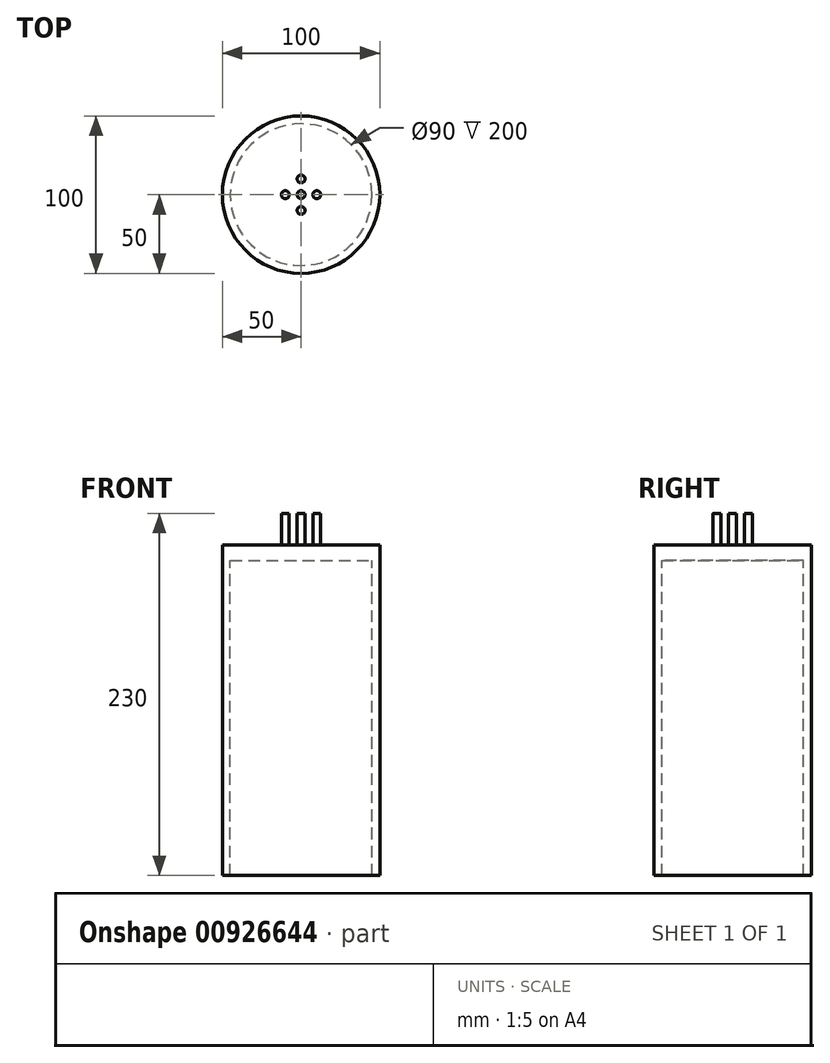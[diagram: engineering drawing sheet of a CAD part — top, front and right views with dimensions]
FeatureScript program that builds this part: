
annotation { "Feature Type Name" : "Feature", "Feature Type Description" : "" }
export const myFeature = defineFeature(function(context is Context, id is Id, definition is map)
    precondition{}
    {
        {
            var Q0;
            Q0=qCreatedBy(makeId("Top.planeOp"),FACE);
            var sketch = newSketch(context, id + "F0", { "sketchPlane" : qUnion([Q0])});
            skCircle(sketch, "E0", {"center": v(0, 0) * mm, "radius": 50 * mm});
            skSolve(sketch);
        }
        {
            var Q0;
            Q0=makeQuery(id+"F0.imprint","IMPRINT",FACE,{"disambiguationData":[TD([[makeQuery(id+"F0.imprint","IMPRINT",EDGE,{"derivedFrom":sQuery(id+"F0.wireOp",EDGE,"E0")}),1.0]])]});
            extrude(context, id + "F1", {"entities" : qUnion([Q0]), "depth" : 10 * mm, "offsetDistance" : 25 * mm});
        }
        {
            var Q0;
            Q0=makeQuery(id+"F1.opExtrude","CAP_FACE",FACE,{"disambiguationData":[OSD([sQuery(id+"F0.wireOp",EDGE,"E0")])],"isStart":true});
            var sketch = newSketch(context, id + "F2", { "sketchPlane" : qUnion([Q0])});
            skCircle(sketch, "E1", {"center": v(0, 0) * mm, "radius": 45 * mm});
            skSolve(sketch);
        }
        {
            var Q0;
            Q0=makeQuery(id+"F2.imprint","IMPRINT",FACE,{"disambiguationData":[TD([[makeQuery(id+"F2.imprint","IMPRINT",EDGE,{"derivedFrom":sQuery(id+"F2.wireOp",EDGE,"E1")}),-1.0]])]});
            extrude(context, id + "F3", {"entities" : qUnion([Q0]), "operationType" : NewBodyOperationType.ADD, "depth" : 200 * mm, "offsetDistance" : 25 * mm});
        }
        {
            var Q0;
            Q0=makeQuery(id+"F1.opExtrude","CAP_FACE",FACE,{"disambiguationData":[OSD([sQuery(id+"F0.wireOp",EDGE,"E0")])],"isStart":false});
            var sketch = newSketch(context, id + "F4", { "sketchPlane" : qUnion([Q0])});
            skCircle(sketch, "E2", {"center": v(0, 0) * mm, "radius": 2.5 * mm});
            skCircle(sketch, "E3", {"center": v(10, 0) * mm, "radius": 2.5 * mm});
            skCircle(sketch, "E4", {"center": v(0, 10) * mm, "radius": 2.5 * mm});
            skCircle(sketch, "E5", {"center": v(-10, 0) * mm, "radius": 2.5 * mm});
            skCircle(sketch, "E6", {"center": v(0, -10) * mm, "radius": 2.5 * mm});
            skSolve(sketch);
        }
        {
            var Q0;
            Q0=makeQuery(id+"F4.imprint","IMPRINT",FACE,{"disambiguationData":[TD([[makeQuery(id+"F4.imprint","IMPRINT",EDGE,{"derivedFrom":sQuery(id+"F4.wireOp",EDGE,"E2")}),1.0]])]});
            var Q1;
            Q1=makeQuery(id+"F4.imprint","IMPRINT",FACE,{"disambiguationData":[TD([[makeQuery(id+"F4.imprint","IMPRINT",EDGE,{"derivedFrom":sQuery(id+"F4.wireOp",EDGE,"E5")}),1.0]])]});
            var Q2;
            Q2=makeQuery(id+"F4.imprint","IMPRINT",FACE,{"disambiguationData":[TD([[makeQuery(id+"F4.imprint","IMPRINT",EDGE,{"derivedFrom":sQuery(id+"F4.wireOp",EDGE,"E4")}),1.0]])]});
            var Q3;
            Q3=makeQuery(id+"F4.imprint","IMPRINT",FACE,{"disambiguationData":[TD([[makeQuery(id+"F4.imprint","IMPRINT",EDGE,{"derivedFrom":sQuery(id+"F4.wireOp",EDGE,"E3")}),1.0]])]});
            var Q4;
            Q4=makeQuery(id+"F4.imprint","IMPRINT",FACE,{"disambiguationData":[TD([[makeQuery(id+"F4.imprint","IMPRINT",EDGE,{"derivedFrom":sQuery(id+"F4.wireOp",EDGE,"E6")}),1.0]])]});
            extrude(context, id + "F5", {"entities" : qUnion([Q0, Q1, Q2, Q3, Q4]), "operationType" : NewBodyOperationType.ADD, "depth" : 20 * mm, "offsetDistance" : 25 * mm});
        }
    });
